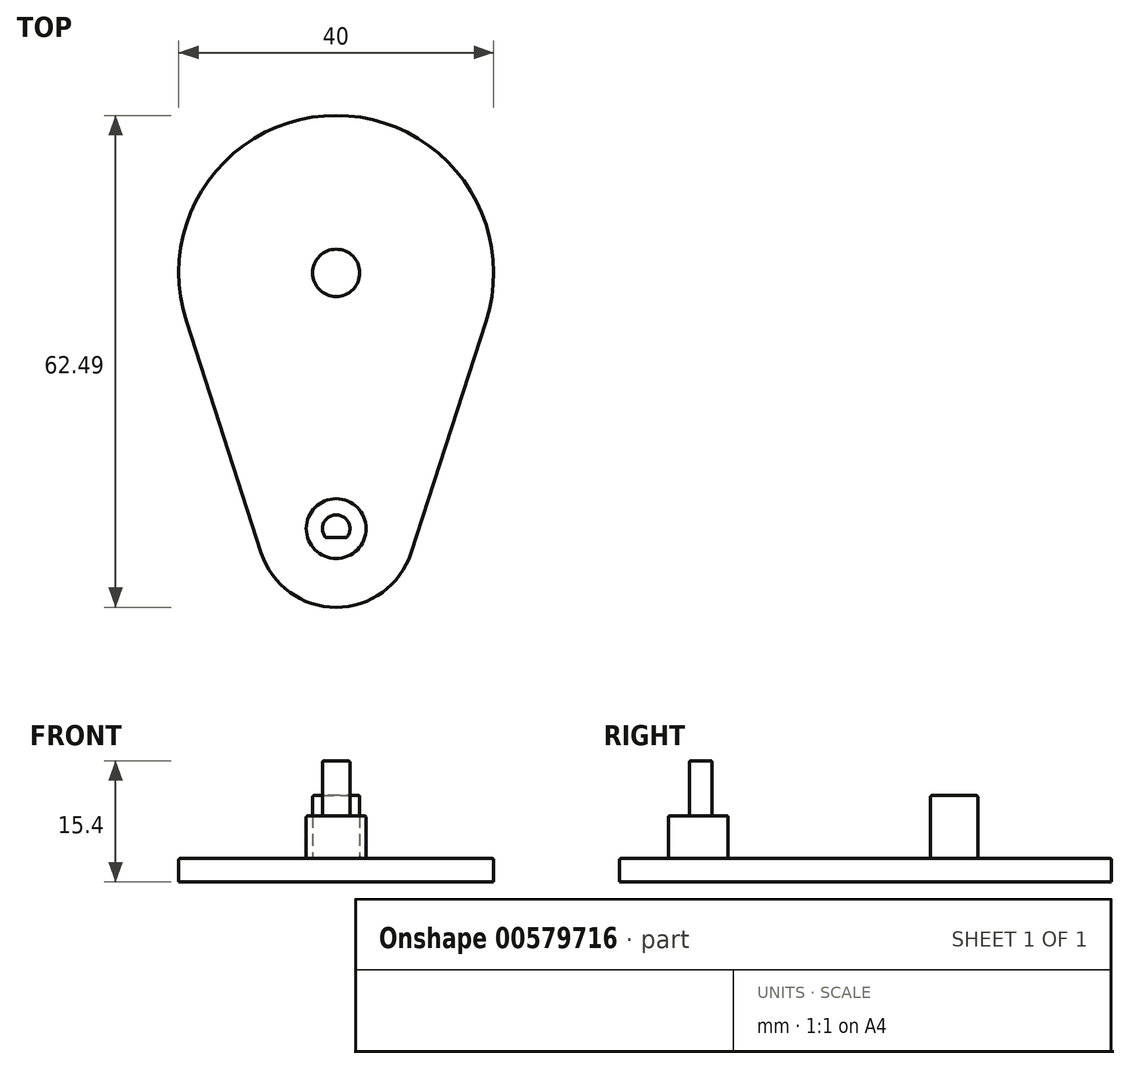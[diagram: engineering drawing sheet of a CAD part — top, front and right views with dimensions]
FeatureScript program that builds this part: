
annotation { "Feature Type Name" : "Feature", "Feature Type Description" : "" }
export const myFeature = defineFeature(function(context is Context, id is Id, definition is map)
    precondition{}
    {
        {
            var Q0;
            Q0=qCreatedBy(makeId("Top.planeOp"),FACE);
            var sketch = newSketch(context, id + "F0", { "sketchPlane" : qUnion([Q0])});
            skCircle(sketch, "E0", {"center": v(0, 32.5) * mm, "radius": 20 * mm});
            skCircle(sketch, "E1", {"center": v(0, 0) * mm, "radius": 10 * mm});
            skLineSegment(sketch, "E2", {"start": v(-9.51, -3.08) * mm, "end": v(-19.03, 26.34) * mm});
            skLineSegment(sketch, "E3", {"start": v(9.51, -3.08) * mm, "end": v(19.03, 26.34) * mm});
            skSolve(sketch);
        }
        {
            var Q0;
            {var subQ0=sQuery(id+"F0.wireOp",EDGE,"E0");var subQ1=makeQuery(id+"F0.imprint","INTERSECT",VERTEX,{"derivedFrom":[subQ0,sQuery(id+"F0.wireOp",EDGE,"E2")]});Q0=makeQuery(id+"F0.imprint","IMPRINT",FACE,{"disambiguationData":[TD([[makeQuery(id+"F0.imprint","IMPRINT",EDGE,{"disambiguationData":[TD([[subQ1,-1.0]])],"derivedFrom":subQ0}),1.0]])]});}
            var Q1;
            {var subQ0=sQuery(id+"F0.wireOp",EDGE,"E1");var subQ1=makeQuery(id+"F0.imprint","INTERSECT",VERTEX,{"derivedFrom":[subQ0,sQuery(id+"F0.wireOp",EDGE,"E2")]});Q1=makeQuery(id+"F0.imprint","IMPRINT",FACE,{"disambiguationData":[TD([[makeQuery(id+"F0.imprint","IMPRINT",EDGE,{"disambiguationData":[TD([[subQ1,1.0]])],"derivedFrom":subQ0}),1.0]])]});}
            var Q2;
            {var subQ0=sQuery(id+"F0.wireOp",EDGE,"E2");Q2=makeQuery(id+"F0.imprint","IMPRINT",FACE,{"disambiguationData":[TD([[makeQuery(id+"F0.imprint","IMPRINT",EDGE,{"derivedFrom":subQ0}),-1.0]])]});}
            extrude(context, id + "F1", {"entities" : qUnion([Q0, Q1, Q2]), "depth" : 3 * mm, "offsetDistance" : 25 * mm});
        }
        {
            var Q0;
            Q0=makeQuery(id+"F1.opExtrude","CAP_FACE",FACE,{"disambiguationData":[OSD([sQuery(id+"F0.wireOp",EDGE,"E0")])],"isStart":false});
            var sketch = newSketch(context, id + "F2", { "sketchPlane" : qUnion([Q0])});
            skCircle(sketch, "E4", {"center": v(0, 32.5) * mm, "radius": 3 * mm});
            skSolve(sketch);
        }
        {
            var Q0;
            Q0=makeQuery(id+"F2.imprint","IMPRINT",FACE,{"disambiguationData":[TD([[makeQuery(id+"F2.imprint","IMPRINT",EDGE,{"derivedFrom":sQuery(id+"F2.wireOp",EDGE,"E4")}),1.0]])]});
            extrude(context, id + "F3", {"entities" : qUnion([Q0]), "operationType" : NewBodyOperationType.ADD, "depth" : 8 * mm, "offsetDistance" : 25 * mm});
        }
        {
            var Q0;
            Q0=makeQuery(id+"F1.opExtrude","CAP_FACE",FACE,{"disambiguationData":[OSD([sQuery(id+"F0.wireOp",EDGE,"E1")])],"isStart":false});
            var sketch = newSketch(context, id + "F4", { "sketchPlane" : qUnion([Q0])});
            skCircle(sketch, "E5", {"center": v(0, 0) * mm, "radius": 3.8 * mm});
            skSolve(sketch);
        }
        {
            var Q0;
            Q0=makeQuery(id+"F4.imprint","IMPRINT",FACE,{"disambiguationData":[TD([[makeQuery(id+"F4.imprint","IMPRINT",EDGE,{"derivedFrom":sQuery(id+"F4.wireOp",EDGE,"E5")}),1.0]])]});
            extrude(context, id + "F5", {"entities" : qUnion([Q0]), "operationType" : NewBodyOperationType.ADD, "depth" : 5.4 * mm, "offsetDistance" : 25 * mm});
        }
        {
            var Q0;
            Q0=makeQuery(id+"F5.opExtrude","CAP_FACE",FACE,{"disambiguationData":[OSD([sQuery(id+"F4.wireOp",EDGE,"E5")])],"isStart":false});
            var sketch = newSketch(context, id + "F6", { "sketchPlane" : qUnion([Q0])});
            skCircle(sketch, "E6", {"center": v(0, 0) * mm, "radius": 1.75 * mm});
            skLineSegment(sketch, "E7", {"start": v(-1.32, -1.15) * mm, "end": v(1.32, -1.15) * mm});
            skSolve(sketch);
        }
        {
            var Q0;
            {var subQ0=sQuery(id+"F6.wireOp",EDGE,"E7");Q0=makeQuery(id+"F6.imprint","IMPRINT",FACE,{"disambiguationData":[TD([[makeQuery(id+"F6.imprint","IMPRINT",EDGE,{"derivedFrom":subQ0}),1.0]])]});}
            extrude(context, id + "F7", {"entities" : qUnion([Q0]), "operationType" : NewBodyOperationType.ADD, "depth" : 7 * mm, "offsetDistance" : 25 * mm});
        }
        {
            var Q0;
            Q0=makeQuery(id+"F3.opExtrude","CAP_FACE",FACE,{"disambiguationData":[OSD([sQuery(id+"F2.wireOp",EDGE,"E4")])],"isStart":false});
            var Q1;
            Q1=makeQuery(id+"F7.opExtrude","CAP_FACE",FACE,{"disambiguationData":[OSD([sQuery(id+"F6.wireOp",EDGE,"E6"),sQuery(id+"F6.wireOp",EDGE,"E7")])],"isStart":false});
            var Q2;
            Q2=makeQuery(id+"F5.opExtrude","CAP_FACE",FACE,{"disambiguationData":[OSD([sQuery(id+"F4.wireOp",EDGE,"E5")])],"isStart":false});
            var Q3;
            Q3=makeQuery(id+"F1.opExtrude","CAP_FACE",FACE,{"disambiguationData":[OSD([sQuery(id+"F0.wireOp",EDGE,"E0"),sQuery(id+"F0.wireOp",EDGE,"E1"),sQuery(id+"F0.wireOp",EDGE,"E2"),sQuery(id+"F0.wireOp",EDGE,"E3")])],"isStart":false});
            var Q4;
            Q4=makeQuery(id+"F7.opExtrude","SWEPT_FACE",FACE,{"disambiguationData":[OSD([sQuery(id+"F6.wireOp",EDGE,"E7")])]});
            fillet(context, id + "F8", {"entities" : qUnion([Q0, Q1, Q2, Q3, Q4]), "radius" : 0.2 * mm, "tangentPropagation" : true, "allowEdgeOverflow" : false});
        }
    });
